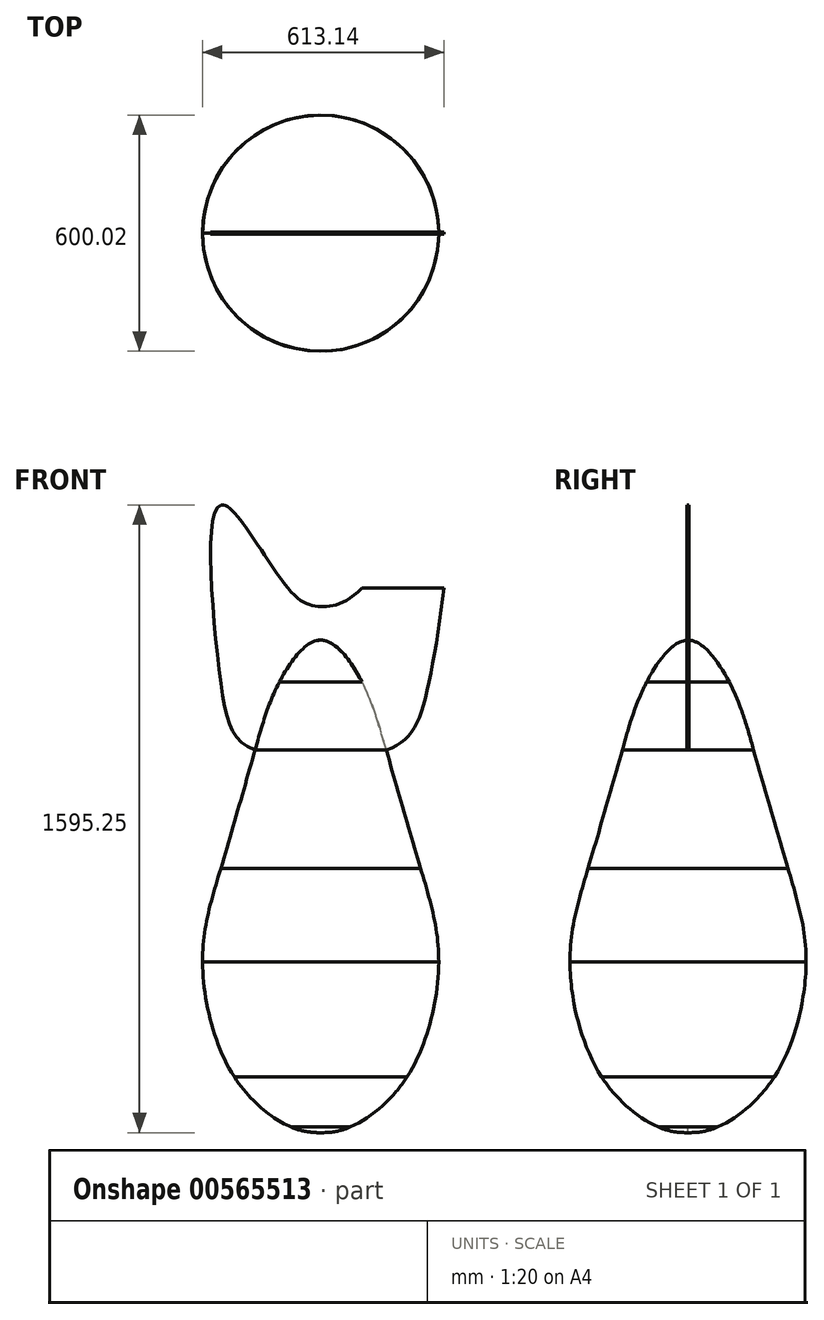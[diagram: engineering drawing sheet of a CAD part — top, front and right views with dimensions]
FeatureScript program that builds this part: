
annotation { "Feature Type Name" : "Feature", "Feature Type Description" : "" }
export const myFeature = defineFeature(function(context is Context, id is Id, definition is map)
    precondition{}
    {
        {
            var Q0;
            Q0=qCreatedBy(makeId("Front.planeOp"),FACE);
            var sketch = newSketch(context, id + "F0", { "sketchPlane" : qUnion([Q0])});
            skFitSpline(sketch, "E0", {"points": [v(0, 0) * mm, v(-75, 14.12) * mm, v(-219.34, 141.7) * mm, v(-300, 433.96) * mm, v(-253.65, 671.97) * mm, v(-166.9, 971.7) * mm, v(-104.82, 1145.07) * mm, v(0, 1251.46) * mm, v(104.82, 1145.07) * mm, v(166.9, 971.7) * mm, v(275, 671.97) * mm, v(300, 433.96) * mm, v(219.34, 141.7) * mm, v(75, 14.12) * mm, v(0, 0) * mm]});
            skLineSegment(sketch, "E1", {"start": v(-75, 14.12) * mm, "end": v(0, 14.12) * mm});
            skLineSegment(sketch, "E2", {"start": v(0, 14.12) * mm, "end": v(75, 14.12) * mm});
            skLineSegment(sketch, "E3", {"start": v(-219.34, 141.7) * mm, "end": v(0, 141.7) * mm});
            skLineSegment(sketch, "E4", {"start": v(0, 141.7) * mm, "end": v(219.34, 141.7) * mm});
            skLineSegment(sketch, "E5", {"start": v(0, 433.96) * mm, "end": v(-300, 433.96) * mm});
            skLineSegment(sketch, "E6", {"start": v(0, 0) * mm, "end": v(0, 1251.46) * mm});
            skLineSegment(sketch, "E7", {"start": v(0, 671.97) * mm, "end": v(-275, 671.97) * mm});
            skLineSegment(sketch, "E8", {"start": v(0, 971.7) * mm, "end": v(-166.9, 971.7) * mm});
            skLineSegment(sketch, "E9", {"start": v(-104.82, 1145.07) * mm, "end": v(0, 1145.07) * mm});
            skLineSegment(sketch, "E10.MirrorCS", {"start": v(104.82, 1145.07) * mm, "end": v(0, 1145.07) * mm});
            skLineSegment(sketch, "E11.MirrorCS", {"start": v(0, 971.7) * mm, "end": v(166.9, 971.7) * mm});
            skLineSegment(sketch, "E12.MirrorCS", {"start": v(0, 671.97) * mm, "end": v(275, 671.97) * mm});
            skLineSegment(sketch, "E13.MirrorCS", {"start": v(0, 433.96) * mm, "end": v(300, 433.96) * mm});
            skPoint(sketch, "E14.6.internal.snap0", {"position": v(-83.45, 971.7) * mm});
            skFitSpline(sketch, "E14", {"points": [v(-166.9, 971.7) * mm, v(166.9, 971.7) * mm, v(275, 1145.07) * mm, v(300, 1595.25) * mm, v(104.82, 1383.7) * mm, v(0, 1336.68) * mm, v(-83.45, 1383.7) * mm, v(-253.65, 1595.25) * mm, v(-253.65, 1145.07) * mm, v(-166.9, 971.7) * mm]});
            skLineSegment(sketch, "E15", {"start": v(-253.65, 1595.25) * mm, "end": v(792.4, 1595.25) * mm});
            skLineSegment(sketch, "E16", {"start": v(-83.45, 1383.7) * mm, "end": v(657.24, 1383.7) * mm});
            skSolve(sketch);
        }
        {
            var Q0;
            {var subQ0=sQuery(id+"F0.wireOp",EDGE,"E1");Q0=makeQuery(id+"F0.imprint","IMPRINT",FACE,{"disambiguationData":[TD([[makeQuery(id+"F0.imprint","IMPRINT",EDGE,{"derivedFrom":subQ0}),1.0]])]});}
            var Q1;
            {var subQ0=sQuery(id+"F0.wireOp",EDGE,"E3");Q1=makeQuery(id+"F0.imprint","IMPRINT",FACE,{"disambiguationData":[TD([[makeQuery(id+"F0.imprint","IMPRINT",EDGE,{"derivedFrom":subQ0}),1.0]])]});}
            var Q2;
            {var subQ0=sQuery(id+"F0.wireOp",EDGE,"E5");Q2=makeQuery(id+"F0.imprint","IMPRINT",FACE,{"disambiguationData":[TD([[makeQuery(id+"F0.imprint","IMPRINT",EDGE,{"derivedFrom":subQ0}),-1.0]])]});}
            var Q3;
            {var subQ0=sQuery(id+"F0.wireOp",EDGE,"E8");Q3=makeQuery(id+"F0.imprint","IMPRINT",FACE,{"disambiguationData":[TD([[makeQuery(id+"F0.imprint","IMPRINT",EDGE,{"derivedFrom":subQ0}),1.0]])]});}
            var Q4;
            {var subQ0=sQuery(id+"F0.wireOp",EDGE,"E8");Q4=makeQuery(id+"F0.imprint","IMPRINT",FACE,{"disambiguationData":[TD([[makeQuery(id+"F0.imprint","IMPRINT",EDGE,{"derivedFrom":subQ0}),-1.0]])]});}
            var Q5;
            {var subQ3=sQuery(id+"F0.wireOp",EDGE,"E9");Q5=makeQuery(id+"F0.imprint","IMPRINT",FACE,{"disambiguationData":[TD([[makeQuery(id+"F0.imprint","IMPRINT",EDGE,{"derivedFrom":subQ3}),1.0]])]});}
            var Q6;
            {var subQ0=sQuery(id+"F0.wireOp",EDGE,"E1");Q6=makeQuery(id+"F0.imprint","IMPRINT",FACE,{"disambiguationData":[TD([[makeQuery(id+"F0.imprint","IMPRINT",EDGE,{"derivedFrom":subQ0}),-1.0]])]});}
            var Q7;
            {var subQ1=sQuery(id+"F0.wireOp",EDGE,"E0");var subQ3=sQuery(id+"F0.wireOp",EDGE,"E7");var subQ4=makeQuery(id+"F0.imprint","INTERSECT",VERTEX,{"derivedFrom":[subQ1,subQ3]});Q7=makeQuery(id+"F0.imprint","IMPRINT",FACE,{"disambiguationData":[TD([[makeQuery(id+"F0.imprint","IMPRINT",EDGE,{"disambiguationData":[TD([[subQ4,-1.0]])],"derivedFrom":subQ1}),-1.0]])]});}
            var Q8;
            Q8=sQuery(id+"F0.wireOp",EDGE,"E6");
            revolve(context, id + "F1", {"entities" : qUnion([Q0, Q1, Q2, Q3, Q4, Q5, Q6, Q7]), "axis" : qUnion([Q8]), "revolveType" : RevolveType.FULL});
        }
        {
            var Q0;
            {var subQ0=sQuery(id+"F0.wireOp",EDGE,"E0");var subQ8=makeQuery(id+"F0.imprint","INTERSECT",VERTEX,{"disambiguationData":[OD(1.0)],"derivedFrom":[subQ0,sQuery(id+"F0.wireOp",EDGE,"E6")]});Q0=makeQuery(id+"F0.imprint","IMPRINT",FACE,{"disambiguationData":[TD([[makeQuery(id+"F0.imprint","IMPRINT",EDGE,{"disambiguationData":[TD([[subQ8,1.0]])],"derivedFrom":subQ0}),1.0]])]});}
            var Q1;
            {var subQ0=sQuery(id+"F0.wireOp",EDGE,"E16");var subQ1=sQuery(id+"F0.wireOp",EDGE,"E14");var subQ2=makeQuery(id+"F0.imprint","INTERSECT",VERTEX,{"disambiguationData":[OD(1.0)],"derivedFrom":[subQ1,subQ0]});Q1=makeQuery(id+"F0.imprint","IMPRINT",FACE,{"disambiguationData":[TD([[makeQuery(id+"F0.imprint","IMPRINT",EDGE,{"disambiguationData":[TD([[subQ2,-1.0]])],"derivedFrom":subQ1}),1.0]])]});}
            extrude(context, id + "F2", {"entities" : qUnion([Q0, Q1]), "depth" : 2.5 * mm, "offsetDistance" : 25 * mm, "hasSecondDirection" : true, "secondDirectionOppositeDirection" : true, "secondDirectionDepth" : 2.5 * mm});
        }
    });
